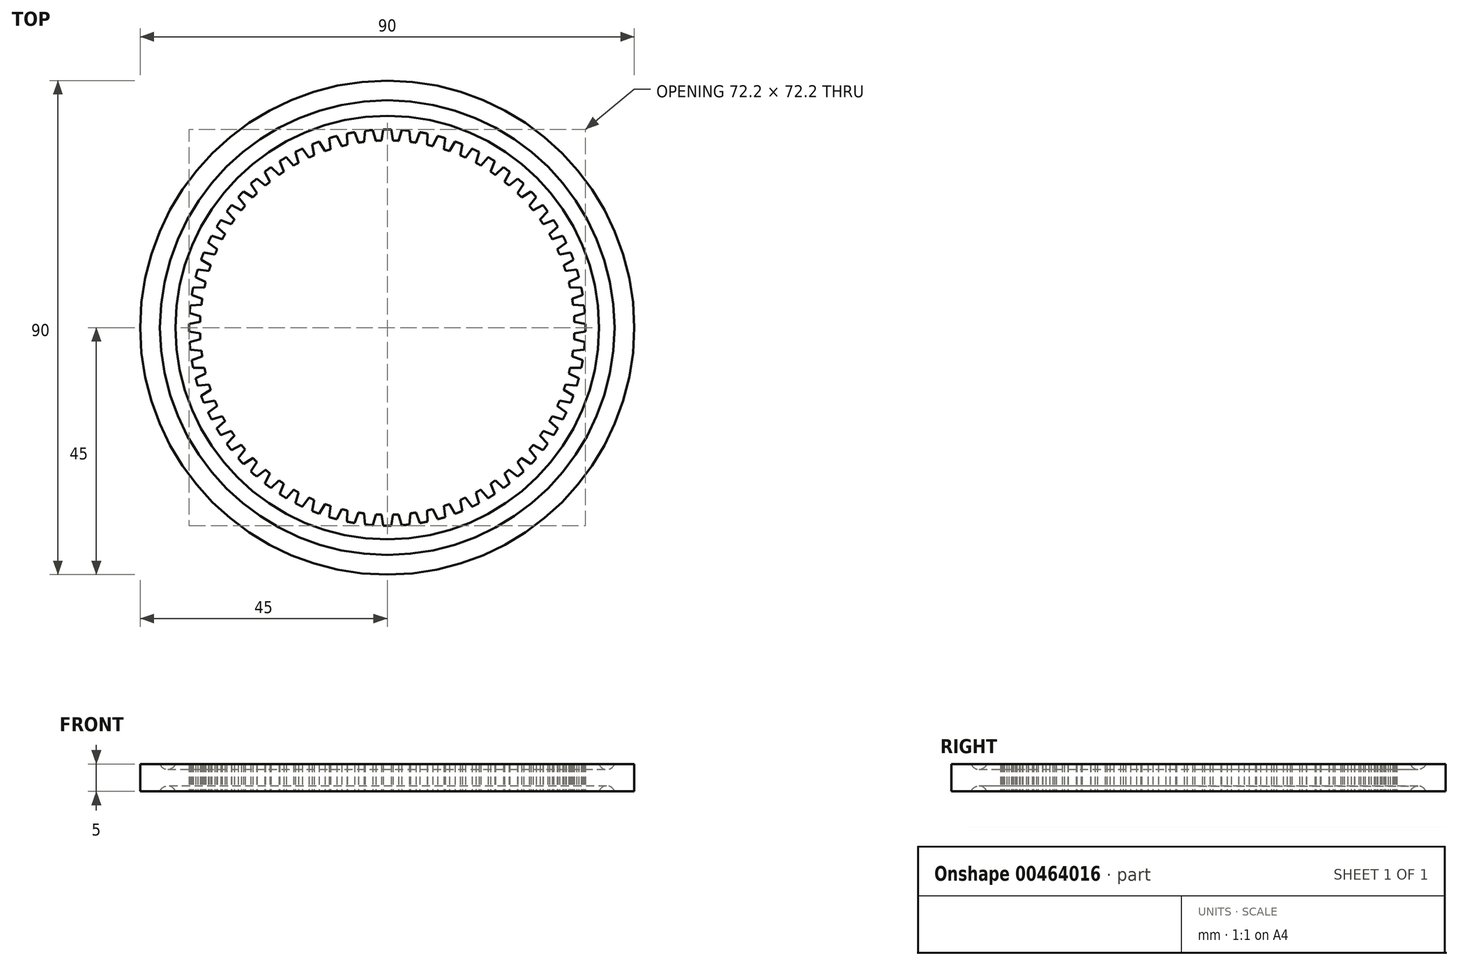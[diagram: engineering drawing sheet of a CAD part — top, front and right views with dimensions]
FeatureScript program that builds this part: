
annotation { "Feature Type Name" : "Feature", "Feature Type Description" : "" }
export const myFeature = defineFeature(function(context is Context, id is Id, definition is map)
    precondition{}
    {
        {
            var Q0;
            Q0=qCreatedBy(makeId("Top.planeOp"),FACE);
            var sketch = newSketch(context, id + "F0", { "sketchPlane" : qUnion([Q0])});
            skCircle(sketch, "E0", {"center": v(0, 0) * mm, "radius": 34.74 * mm, "construction": true});
            skCircle(sketch, "E1", {"center": v(0, 0) * mm, "radius": 45 * mm});
            skLineSegment(sketch, "E2", {"start": v(-0.94, 0) * mm, "end": v(-0.94, 34.7) * mm, "construction": true});
            skLineSegment(sketch, "E3", {"start": v(0.94, 0) * mm, "end": v(0.94, 34.7) * mm, "construction": true});
            skLineSegment(sketch, "E4", {"start": v(0, 0) * mm, "end": v(0, 34.8) * mm, "construction": true});
            skPoint(sketch, "E5", {"position": v(0.94, 34.73) * mm});
            skPoint(sketch, "E6", {"position": v(-0.94, 34.73) * mm});
            skLineSegment(sketch, "E7", {"start": v(0.94, 34.73) * mm, "end": v(1.06, 34.08) * mm});
            skLineSegment(sketch, "E8", {"start": v(0.94, 34.73) * mm, "end": v(0.7, 36.1) * mm});
            skLineSegment(sketch, "E9.MirrorCS", {"start": v(-0.94, 34.73) * mm, "end": v(-1.06, 34.08) * mm});
            skLineSegment(sketch, "E10.MirrorCS", {"start": v(-0.94, 34.73) * mm, "end": v(-0.7, 36.1) * mm});
            skLineSegment(sketch, "E11.1.0", {"start": v(-4.14, 34.5) * mm, "end": v(-4.2, 33.84) * mm});
            skLineSegment(sketch, "E11.1.1", {"start": v(-4.14, 34.5) * mm, "end": v(-4.03, 35.87) * mm});
            skLineSegment(sketch, "E11.1.2", {"start": v(-2.27, 34.67) * mm, "end": v(-2.63, 36) * mm});
            skLineSegment(sketch, "E11.1.3", {"start": v(-2.27, 34.67) * mm, "end": v(-2.1, 34.04) * mm});
            skLineSegment(sketch, "E11.2.0", {"start": v(-7.3, 33.96) * mm, "end": v(-7.3, 33.3) * mm});
            skLineSegment(sketch, "E11.2.1", {"start": v(-7.3, 33.96) * mm, "end": v(-7.32, 35.35) * mm});
            skLineSegment(sketch, "E11.2.2", {"start": v(-5.45, 34.3) * mm, "end": v(-5.94, 35.6) * mm});
            skLineSegment(sketch, "E11.2.3", {"start": v(-5.45, 34.3) * mm, "end": v(-5.22, 33.7) * mm});
            skLineSegment(sketch, "E11.3.0", {"start": v(-10.41, 33.14) * mm, "end": v(-10.34, 32.5) * mm});
            skLineSegment(sketch, "E11.3.1", {"start": v(-10.41, 33.14) * mm, "end": v(-10.55, 34.52) * mm});
            skLineSegment(sketch, "E11.3.2", {"start": v(-8.6, 33.66) * mm, "end": v(-9.2, 34.9) * mm});
            skLineSegment(sketch, "E11.3.3", {"start": v(-8.6, 33.66) * mm, "end": v(-8.31, 33.07) * mm});
            skLineSegment(sketch, "E11.4.0", {"start": v(-13.42, 32.04) * mm, "end": v(-13.3, 31.4) * mm});
            skLineSegment(sketch, "E11.4.1", {"start": v(-13.42, 32.04) * mm, "end": v(-13.7, 33.4) * mm});
            skLineSegment(sketch, "E11.4.2", {"start": v(-11.67, 32.72) * mm, "end": v(-12.38, 33.9) * mm});
            skLineSegment(sketch, "E11.4.3", {"start": v(-11.67, 32.72) * mm, "end": v(-11.33, 32.16) * mm});
            skLineSegment(sketch, "E11.5.0", {"start": v(-16.32, 30.67) * mm, "end": v(-16.14, 30.04) * mm});
            skLineSegment(sketch, "E11.5.1", {"start": v(-16.32, 30.67) * mm, "end": v(-16.72, 32) * mm});
            skLineSegment(sketch, "E11.5.2", {"start": v(-14.64, 31.5) * mm, "end": v(-15.46, 32.62) * mm});
            skLineSegment(sketch, "E11.5.3", {"start": v(-14.64, 31.5) * mm, "end": v(-14.25, 30.98) * mm});
            skLineSegment(sketch, "E11.6.0", {"start": v(-19.08, 29.03) * mm, "end": v(-18.84, 28.42) * mm});
            skLineSegment(sketch, "E11.6.1", {"start": v(-19.08, 29.03) * mm, "end": v(-19.6, 30.32) * mm});
            skLineSegment(sketch, "E11.6.2", {"start": v(-17.48, 30.02) * mm, "end": v(-18.4, 31.06) * mm});
            skLineSegment(sketch, "E11.6.3", {"start": v(-17.48, 30.02) * mm, "end": v(-17.04, 29.53) * mm});
            skLineSegment(sketch, "E11.7.0", {"start": v(-21.68, 27.15) * mm, "end": v(-21.38, 26.56) * mm});
            skLineSegment(sketch, "E11.7.1", {"start": v(-21.68, 27.15) * mm, "end": v(-22.31, 28.38) * mm});
            skLineSegment(sketch, "E11.7.2", {"start": v(-20.18, 28.28) * mm, "end": v(-21.2, 29.23) * mm});
            skLineSegment(sketch, "E11.7.3", {"start": v(-20.18, 28.28) * mm, "end": v(-19.7, 27.84) * mm});
            skLineSegment(sketch, "E11.8.0", {"start": v(-24.1, 25.03) * mm, "end": v(-23.74, 24.48) * mm});
            skLineSegment(sketch, "E11.8.1", {"start": v(-24.1, 25.03) * mm, "end": v(-24.83, 26.2) * mm});
            skLineSegment(sketch, "E11.8.2", {"start": v(-22.7, 26.3) * mm, "end": v(-23.8, 27.15) * mm});
            skLineSegment(sketch, "E11.8.3", {"start": v(-22.7, 26.3) * mm, "end": v(-22.18, 25.9) * mm});
            skLineSegment(sketch, "E11.9.0", {"start": v(-26.3, 22.7) * mm, "end": v(-25.9, 22.18) * mm});
            skLineSegment(sketch, "E11.9.1", {"start": v(-26.3, 22.7) * mm, "end": v(-27.15, 23.8) * mm});
            skLineSegment(sketch, "E11.9.2", {"start": v(-25.03, 24.1) * mm, "end": v(-26.2, 24.83) * mm});
            skLineSegment(sketch, "E11.9.3", {"start": v(-25.03, 24.1) * mm, "end": v(-24.48, 23.74) * mm});
            skLineSegment(sketch, "E11.10.0", {"start": v(-28.28, 20.18) * mm, "end": v(-27.84, 19.7) * mm});
            skLineSegment(sketch, "E11.10.1", {"start": v(-28.28, 20.18) * mm, "end": v(-29.23, 21.2) * mm});
            skLineSegment(sketch, "E11.10.2", {"start": v(-27.15, 21.68) * mm, "end": v(-28.38, 22.31) * mm});
            skLineSegment(sketch, "E11.10.3", {"start": v(-27.15, 21.68) * mm, "end": v(-26.56, 21.38) * mm});
            skLineSegment(sketch, "E11.11.0", {"start": v(-30.02, 17.48) * mm, "end": v(-29.53, 17.04) * mm});
            skLineSegment(sketch, "E11.11.1", {"start": v(-30.02, 17.48) * mm, "end": v(-31.06, 18.4) * mm});
            skLineSegment(sketch, "E11.11.2", {"start": v(-29.03, 19.08) * mm, "end": v(-30.32, 19.6) * mm});
            skLineSegment(sketch, "E11.11.3", {"start": v(-29.03, 19.08) * mm, "end": v(-28.42, 18.84) * mm});
            skLineSegment(sketch, "E11.12.0", {"start": v(-31.5, 14.64) * mm, "end": v(-30.98, 14.25) * mm});
            skLineSegment(sketch, "E11.12.1", {"start": v(-31.5, 14.64) * mm, "end": v(-32.62, 15.46) * mm});
            skLineSegment(sketch, "E11.12.2", {"start": v(-30.67, 16.32) * mm, "end": v(-32, 16.72) * mm});
            skLineSegment(sketch, "E11.12.3", {"start": v(-30.67, 16.32) * mm, "end": v(-30.04, 16.14) * mm});
            skLineSegment(sketch, "E11.13.0", {"start": v(-32.72, 11.67) * mm, "end": v(-32.16, 11.33) * mm});
            skLineSegment(sketch, "E11.13.1", {"start": v(-32.72, 11.67) * mm, "end": v(-33.9, 12.38) * mm});
            skLineSegment(sketch, "E11.13.2", {"start": v(-32.04, 13.42) * mm, "end": v(-33.4, 13.7) * mm});
            skLineSegment(sketch, "E11.13.3", {"start": v(-32.04, 13.42) * mm, "end": v(-31.4, 13.3) * mm});
            skLineSegment(sketch, "E11.14.0", {"start": v(-33.66, 8.6) * mm, "end": v(-33.07, 8.31) * mm});
            skLineSegment(sketch, "E11.14.1", {"start": v(-33.66, 8.6) * mm, "end": v(-34.9, 9.2) * mm});
            skLineSegment(sketch, "E11.14.2", {"start": v(-33.14, 10.41) * mm, "end": v(-34.52, 10.55) * mm});
            skLineSegment(sketch, "E11.14.3", {"start": v(-33.14, 10.41) * mm, "end": v(-32.5, 10.34) * mm});
            skLineSegment(sketch, "E11.15.0", {"start": v(-34.3, 5.45) * mm, "end": v(-33.7, 5.22) * mm});
            skLineSegment(sketch, "E11.15.1", {"start": v(-34.3, 5.45) * mm, "end": v(-35.6, 5.94) * mm});
            skLineSegment(sketch, "E11.15.2", {"start": v(-33.96, 7.3) * mm, "end": v(-35.35, 7.32) * mm});
            skLineSegment(sketch, "E11.15.3", {"start": v(-33.96, 7.3) * mm, "end": v(-33.3, 7.3) * mm});
            skLineSegment(sketch, "E11.16.0", {"start": v(-34.67, 2.27) * mm, "end": v(-34.04, 2.1) * mm});
            skLineSegment(sketch, "E11.16.1", {"start": v(-34.67, 2.27) * mm, "end": v(-36, 2.63) * mm});
            skLineSegment(sketch, "E11.16.2", {"start": v(-34.5, 4.14) * mm, "end": v(-35.87, 4.03) * mm});
            skLineSegment(sketch, "E11.16.3", {"start": v(-34.5, 4.14) * mm, "end": v(-33.84, 4.2) * mm});
            skLineSegment(sketch, "E11.17.0", {"start": v(-34.73, -0.94) * mm, "end": v(-34.08, -1.06) * mm});
            skLineSegment(sketch, "E11.17.1", {"start": v(-34.73, -0.94) * mm, "end": v(-36.1, -0.7) * mm});
            skLineSegment(sketch, "E11.17.2", {"start": v(-34.73, 0.94) * mm, "end": v(-36.1, 0.7) * mm});
            skLineSegment(sketch, "E11.17.3", {"start": v(-34.73, 0.94) * mm, "end": v(-34.08, 1.06) * mm});
            skLineSegment(sketch, "E11.18.0", {"start": v(-34.5, -4.14) * mm, "end": v(-33.84, -4.2) * mm});
            skLineSegment(sketch, "E11.18.1", {"start": v(-34.5, -4.14) * mm, "end": v(-35.87, -4.03) * mm});
            skLineSegment(sketch, "E11.18.2", {"start": v(-34.67, -2.27) * mm, "end": v(-36, -2.63) * mm});
            skLineSegment(sketch, "E11.18.3", {"start": v(-34.67, -2.27) * mm, "end": v(-34.04, -2.1) * mm});
            skLineSegment(sketch, "E11.19.0", {"start": v(-33.96, -7.3) * mm, "end": v(-33.3, -7.3) * mm});
            skLineSegment(sketch, "E11.19.1", {"start": v(-33.96, -7.3) * mm, "end": v(-35.35, -7.32) * mm});
            skLineSegment(sketch, "E11.19.2", {"start": v(-34.3, -5.45) * mm, "end": v(-35.6, -5.94) * mm});
            skLineSegment(sketch, "E11.19.3", {"start": v(-34.3, -5.45) * mm, "end": v(-33.7, -5.22) * mm});
            skLineSegment(sketch, "E11.20.0", {"start": v(-33.14, -10.41) * mm, "end": v(-32.5, -10.34) * mm});
            skLineSegment(sketch, "E11.20.1", {"start": v(-33.14, -10.41) * mm, "end": v(-34.52, -10.55) * mm});
            skLineSegment(sketch, "E11.20.2", {"start": v(-33.66, -8.6) * mm, "end": v(-34.9, -9.2) * mm});
            skLineSegment(sketch, "E11.20.3", {"start": v(-33.66, -8.6) * mm, "end": v(-33.07, -8.31) * mm});
            skLineSegment(sketch, "E11.21.0", {"start": v(-32.04, -13.42) * mm, "end": v(-31.4, -13.3) * mm});
            skLineSegment(sketch, "E11.21.1", {"start": v(-32.04, -13.42) * mm, "end": v(-33.4, -13.7) * mm});
            skLineSegment(sketch, "E11.21.2", {"start": v(-32.72, -11.67) * mm, "end": v(-33.9, -12.38) * mm});
            skLineSegment(sketch, "E11.21.3", {"start": v(-32.72, -11.67) * mm, "end": v(-32.16, -11.33) * mm});
            skLineSegment(sketch, "E11.22.0", {"start": v(-30.67, -16.32) * mm, "end": v(-30.04, -16.14) * mm});
            skLineSegment(sketch, "E11.22.1", {"start": v(-30.67, -16.32) * mm, "end": v(-32, -16.72) * mm});
            skLineSegment(sketch, "E11.22.2", {"start": v(-31.5, -14.64) * mm, "end": v(-32.62, -15.46) * mm});
            skLineSegment(sketch, "E11.22.3", {"start": v(-31.5, -14.64) * mm, "end": v(-30.98, -14.25) * mm});
            skLineSegment(sketch, "E11.23.0", {"start": v(-29.03, -19.08) * mm, "end": v(-28.42, -18.84) * mm});
            skLineSegment(sketch, "E11.23.1", {"start": v(-29.03, -19.08) * mm, "end": v(-30.32, -19.6) * mm});
            skLineSegment(sketch, "E11.23.2", {"start": v(-30.02, -17.48) * mm, "end": v(-31.06, -18.4) * mm});
            skLineSegment(sketch, "E11.23.3", {"start": v(-30.02, -17.48) * mm, "end": v(-29.53, -17.04) * mm});
            skLineSegment(sketch, "E11.24.0", {"start": v(-27.15, -21.68) * mm, "end": v(-26.56, -21.38) * mm});
            skLineSegment(sketch, "E11.24.1", {"start": v(-27.15, -21.68) * mm, "end": v(-28.38, -22.31) * mm});
            skLineSegment(sketch, "E11.24.2", {"start": v(-28.28, -20.18) * mm, "end": v(-29.23, -21.2) * mm});
            skLineSegment(sketch, "E11.24.3", {"start": v(-28.28, -20.18) * mm, "end": v(-27.84, -19.7) * mm});
            skLineSegment(sketch, "E11.25.0", {"start": v(-25.03, -24.1) * mm, "end": v(-24.48, -23.74) * mm});
            skLineSegment(sketch, "E11.25.1", {"start": v(-25.03, -24.1) * mm, "end": v(-26.2, -24.83) * mm});
            skLineSegment(sketch, "E11.25.2", {"start": v(-26.3, -22.7) * mm, "end": v(-27.15, -23.8) * mm});
            skLineSegment(sketch, "E11.25.3", {"start": v(-26.3, -22.7) * mm, "end": v(-25.9, -22.18) * mm});
            skLineSegment(sketch, "E11.26.0", {"start": v(-22.7, -26.3) * mm, "end": v(-22.18, -25.9) * mm});
            skLineSegment(sketch, "E11.26.1", {"start": v(-22.7, -26.3) * mm, "end": v(-23.8, -27.15) * mm});
            skLineSegment(sketch, "E11.26.2", {"start": v(-24.1, -25.03) * mm, "end": v(-24.83, -26.2) * mm});
            skLineSegment(sketch, "E11.26.3", {"start": v(-24.1, -25.03) * mm, "end": v(-23.74, -24.48) * mm});
            skLineSegment(sketch, "E11.27.0", {"start": v(-20.18, -28.28) * mm, "end": v(-19.7, -27.84) * mm});
            skLineSegment(sketch, "E11.27.1", {"start": v(-20.18, -28.28) * mm, "end": v(-21.2, -29.23) * mm});
            skLineSegment(sketch, "E11.27.2", {"start": v(-21.68, -27.15) * mm, "end": v(-22.31, -28.38) * mm});
            skLineSegment(sketch, "E11.27.3", {"start": v(-21.68, -27.15) * mm, "end": v(-21.38, -26.56) * mm});
            skLineSegment(sketch, "E11.28.0", {"start": v(-17.48, -30.02) * mm, "end": v(-17.04, -29.53) * mm});
            skLineSegment(sketch, "E11.28.1", {"start": v(-17.48, -30.02) * mm, "end": v(-18.4, -31.06) * mm});
            skLineSegment(sketch, "E11.28.2", {"start": v(-19.08, -29.03) * mm, "end": v(-19.6, -30.32) * mm});
            skLineSegment(sketch, "E11.28.3", {"start": v(-19.08, -29.03) * mm, "end": v(-18.84, -28.42) * mm});
            skLineSegment(sketch, "E11.29.0", {"start": v(-14.64, -31.5) * mm, "end": v(-14.25, -30.98) * mm});
            skLineSegment(sketch, "E11.29.1", {"start": v(-14.64, -31.5) * mm, "end": v(-15.46, -32.62) * mm});
            skLineSegment(sketch, "E11.29.2", {"start": v(-16.32, -30.67) * mm, "end": v(-16.72, -32) * mm});
            skLineSegment(sketch, "E11.29.3", {"start": v(-16.32, -30.67) * mm, "end": v(-16.14, -30.04) * mm});
            skLineSegment(sketch, "E11.30.0", {"start": v(-11.67, -32.72) * mm, "end": v(-11.33, -32.16) * mm});
            skLineSegment(sketch, "E11.30.1", {"start": v(-11.67, -32.72) * mm, "end": v(-12.38, -33.9) * mm});
            skLineSegment(sketch, "E11.30.2", {"start": v(-13.42, -32.04) * mm, "end": v(-13.7, -33.4) * mm});
            skLineSegment(sketch, "E11.30.3", {"start": v(-13.42, -32.04) * mm, "end": v(-13.3, -31.4) * mm});
            skLineSegment(sketch, "E11.31.0", {"start": v(-8.6, -33.66) * mm, "end": v(-8.31, -33.07) * mm});
            skLineSegment(sketch, "E11.31.1", {"start": v(-8.6, -33.66) * mm, "end": v(-9.2, -34.9) * mm});
            skLineSegment(sketch, "E11.31.2", {"start": v(-10.41, -33.14) * mm, "end": v(-10.55, -34.52) * mm});
            skLineSegment(sketch, "E11.31.3", {"start": v(-10.41, -33.14) * mm, "end": v(-10.34, -32.5) * mm});
            skLineSegment(sketch, "E11.32.0", {"start": v(-5.45, -34.3) * mm, "end": v(-5.22, -33.7) * mm});
            skLineSegment(sketch, "E11.32.1", {"start": v(-5.45, -34.3) * mm, "end": v(-5.94, -35.6) * mm});
            skLineSegment(sketch, "E11.32.2", {"start": v(-7.3, -33.96) * mm, "end": v(-7.32, -35.35) * mm});
            skLineSegment(sketch, "E11.32.3", {"start": v(-7.3, -33.96) * mm, "end": v(-7.3, -33.3) * mm});
            skLineSegment(sketch, "E11.33.0", {"start": v(-2.27, -34.67) * mm, "end": v(-2.1, -34.04) * mm});
            skLineSegment(sketch, "E11.33.1", {"start": v(-2.27, -34.67) * mm, "end": v(-2.63, -36) * mm});
            skLineSegment(sketch, "E11.33.2", {"start": v(-4.14, -34.5) * mm, "end": v(-4.03, -35.87) * mm});
            skLineSegment(sketch, "E11.33.3", {"start": v(-4.14, -34.5) * mm, "end": v(-4.2, -33.84) * mm});
            skLineSegment(sketch, "E11.34.0", {"start": v(0.94, -34.73) * mm, "end": v(1.06, -34.08) * mm});
            skLineSegment(sketch, "E11.34.1", {"start": v(0.94, -34.73) * mm, "end": v(0.7, -36.1) * mm});
            skLineSegment(sketch, "E11.34.2", {"start": v(-0.94, -34.73) * mm, "end": v(-0.7, -36.1) * mm});
            skLineSegment(sketch, "E11.34.3", {"start": v(-0.94, -34.73) * mm, "end": v(-1.06, -34.08) * mm});
            skLineSegment(sketch, "E11.35.0", {"start": v(4.14, -34.5) * mm, "end": v(4.2, -33.84) * mm});
            skLineSegment(sketch, "E11.35.1", {"start": v(4.14, -34.5) * mm, "end": v(4.03, -35.87) * mm});
            skLineSegment(sketch, "E11.35.2", {"start": v(2.27, -34.67) * mm, "end": v(2.63, -36) * mm});
            skLineSegment(sketch, "E11.35.3", {"start": v(2.27, -34.67) * mm, "end": v(2.1, -34.04) * mm});
            skLineSegment(sketch, "E11.36.0", {"start": v(7.3, -33.96) * mm, "end": v(7.3, -33.3) * mm});
            skLineSegment(sketch, "E11.36.1", {"start": v(7.3, -33.96) * mm, "end": v(7.32, -35.35) * mm});
            skLineSegment(sketch, "E11.36.2", {"start": v(5.45, -34.3) * mm, "end": v(5.94, -35.6) * mm});
            skLineSegment(sketch, "E11.36.3", {"start": v(5.45, -34.3) * mm, "end": v(5.22, -33.7) * mm});
            skLineSegment(sketch, "E11.37.0", {"start": v(10.41, -33.14) * mm, "end": v(10.34, -32.5) * mm});
            skLineSegment(sketch, "E11.37.1", {"start": v(10.41, -33.14) * mm, "end": v(10.55, -34.52) * mm});
            skLineSegment(sketch, "E11.37.2", {"start": v(8.6, -33.66) * mm, "end": v(9.2, -34.9) * mm});
            skLineSegment(sketch, "E11.37.3", {"start": v(8.6, -33.66) * mm, "end": v(8.31, -33.07) * mm});
            skLineSegment(sketch, "E11.38.0", {"start": v(13.42, -32.04) * mm, "end": v(13.3, -31.4) * mm});
            skLineSegment(sketch, "E11.38.1", {"start": v(13.42, -32.04) * mm, "end": v(13.7, -33.4) * mm});
            skLineSegment(sketch, "E11.38.2", {"start": v(11.67, -32.72) * mm, "end": v(12.38, -33.9) * mm});
            skLineSegment(sketch, "E11.38.3", {"start": v(11.67, -32.72) * mm, "end": v(11.33, -32.16) * mm});
            skLineSegment(sketch, "E11.39.0", {"start": v(16.32, -30.67) * mm, "end": v(16.14, -30.04) * mm});
            skLineSegment(sketch, "E11.39.1", {"start": v(16.32, -30.67) * mm, "end": v(16.72, -32) * mm});
            skLineSegment(sketch, "E11.39.2", {"start": v(14.64, -31.5) * mm, "end": v(15.46, -32.62) * mm});
            skLineSegment(sketch, "E11.39.3", {"start": v(14.64, -31.5) * mm, "end": v(14.25, -30.98) * mm});
            skLineSegment(sketch, "E11.40.0", {"start": v(19.08, -29.03) * mm, "end": v(18.84, -28.42) * mm});
            skLineSegment(sketch, "E11.40.1", {"start": v(19.08, -29.03) * mm, "end": v(19.6, -30.32) * mm});
            skLineSegment(sketch, "E11.40.2", {"start": v(17.48, -30.02) * mm, "end": v(18.4, -31.06) * mm});
            skLineSegment(sketch, "E11.40.3", {"start": v(17.48, -30.02) * mm, "end": v(17.04, -29.53) * mm});
            skLineSegment(sketch, "E11.41.0", {"start": v(21.68, -27.15) * mm, "end": v(21.38, -26.56) * mm});
            skLineSegment(sketch, "E11.41.1", {"start": v(21.68, -27.15) * mm, "end": v(22.31, -28.38) * mm});
            skLineSegment(sketch, "E11.41.2", {"start": v(20.18, -28.28) * mm, "end": v(21.2, -29.23) * mm});
            skLineSegment(sketch, "E11.41.3", {"start": v(20.18, -28.28) * mm, "end": v(19.7, -27.84) * mm});
            skLineSegment(sketch, "E11.42.0", {"start": v(24.1, -25.03) * mm, "end": v(23.74, -24.48) * mm});
            skLineSegment(sketch, "E11.42.1", {"start": v(24.1, -25.03) * mm, "end": v(24.83, -26.2) * mm});
            skLineSegment(sketch, "E11.42.2", {"start": v(22.7, -26.3) * mm, "end": v(23.8, -27.15) * mm});
            skLineSegment(sketch, "E11.42.3", {"start": v(22.7, -26.3) * mm, "end": v(22.18, -25.9) * mm});
            skLineSegment(sketch, "E11.43.0", {"start": v(26.3, -22.7) * mm, "end": v(25.9, -22.18) * mm});
            skLineSegment(sketch, "E11.43.1", {"start": v(26.3, -22.7) * mm, "end": v(27.15, -23.8) * mm});
            skLineSegment(sketch, "E11.43.2", {"start": v(25.03, -24.1) * mm, "end": v(26.2, -24.83) * mm});
            skLineSegment(sketch, "E11.43.3", {"start": v(25.03, -24.1) * mm, "end": v(24.48, -23.74) * mm});
            skLineSegment(sketch, "E11.44.0", {"start": v(28.28, -20.18) * mm, "end": v(27.84, -19.7) * mm});
            skLineSegment(sketch, "E11.44.1", {"start": v(28.28, -20.18) * mm, "end": v(29.23, -21.2) * mm});
            skLineSegment(sketch, "E11.44.2", {"start": v(27.15, -21.68) * mm, "end": v(28.38, -22.31) * mm});
            skLineSegment(sketch, "E11.44.3", {"start": v(27.15, -21.68) * mm, "end": v(26.56, -21.38) * mm});
            skLineSegment(sketch, "E11.45.0", {"start": v(30.02, -17.48) * mm, "end": v(29.53, -17.04) * mm});
            skLineSegment(sketch, "E11.45.1", {"start": v(30.02, -17.48) * mm, "end": v(31.06, -18.4) * mm});
            skLineSegment(sketch, "E11.45.2", {"start": v(29.03, -19.08) * mm, "end": v(30.32, -19.6) * mm});
            skLineSegment(sketch, "E11.45.3", {"start": v(29.03, -19.08) * mm, "end": v(28.42, -18.84) * mm});
            skLineSegment(sketch, "E11.46.0", {"start": v(31.5, -14.64) * mm, "end": v(30.98, -14.25) * mm});
            skLineSegment(sketch, "E11.46.1", {"start": v(31.5, -14.64) * mm, "end": v(32.62, -15.46) * mm});
            skLineSegment(sketch, "E11.46.2", {"start": v(30.67, -16.32) * mm, "end": v(32, -16.72) * mm});
            skLineSegment(sketch, "E11.46.3", {"start": v(30.67, -16.32) * mm, "end": v(30.04, -16.14) * mm});
            skLineSegment(sketch, "E11.47.0", {"start": v(32.72, -11.67) * mm, "end": v(32.16, -11.33) * mm});
            skLineSegment(sketch, "E11.47.1", {"start": v(32.72, -11.67) * mm, "end": v(33.9, -12.38) * mm});
            skLineSegment(sketch, "E11.47.2", {"start": v(32.04, -13.42) * mm, "end": v(33.4, -13.7) * mm});
            skLineSegment(sketch, "E11.47.3", {"start": v(32.04, -13.42) * mm, "end": v(31.4, -13.3) * mm});
            skLineSegment(sketch, "E11.48.0", {"start": v(33.66, -8.6) * mm, "end": v(33.07, -8.31) * mm});
            skLineSegment(sketch, "E11.48.1", {"start": v(33.66, -8.6) * mm, "end": v(34.9, -9.2) * mm});
            skLineSegment(sketch, "E11.48.2", {"start": v(33.14, -10.41) * mm, "end": v(34.52, -10.55) * mm});
            skLineSegment(sketch, "E11.48.3", {"start": v(33.14, -10.41) * mm, "end": v(32.5, -10.34) * mm});
            skLineSegment(sketch, "E11.49.0", {"start": v(34.3, -5.45) * mm, "end": v(33.7, -5.22) * mm});
            skLineSegment(sketch, "E11.49.1", {"start": v(34.3, -5.45) * mm, "end": v(35.6, -5.94) * mm});
            skLineSegment(sketch, "E11.49.2", {"start": v(33.96, -7.3) * mm, "end": v(35.35, -7.32) * mm});
            skLineSegment(sketch, "E11.49.3", {"start": v(33.96, -7.3) * mm, "end": v(33.3, -7.3) * mm});
            skLineSegment(sketch, "E11.50.0", {"start": v(34.67, -2.27) * mm, "end": v(34.04, -2.1) * mm});
            skLineSegment(sketch, "E11.50.1", {"start": v(34.67, -2.27) * mm, "end": v(36, -2.63) * mm});
            skLineSegment(sketch, "E11.50.2", {"start": v(34.5, -4.14) * mm, "end": v(35.87, -4.03) * mm});
            skLineSegment(sketch, "E11.50.3", {"start": v(34.5, -4.14) * mm, "end": v(33.84, -4.2) * mm});
            skLineSegment(sketch, "E11.51.0", {"start": v(34.73, 0.94) * mm, "end": v(34.08, 1.06) * mm});
            skLineSegment(sketch, "E11.51.1", {"start": v(34.73, 0.94) * mm, "end": v(36.1, 0.7) * mm});
            skLineSegment(sketch, "E11.51.2", {"start": v(34.73, -0.94) * mm, "end": v(36.1, -0.7) * mm});
            skLineSegment(sketch, "E11.51.3", {"start": v(34.73, -0.94) * mm, "end": v(34.08, -1.06) * mm});
            skLineSegment(sketch, "E11.52.0", {"start": v(34.5, 4.14) * mm, "end": v(33.84, 4.2) * mm});
            skLineSegment(sketch, "E11.52.1", {"start": v(34.5, 4.14) * mm, "end": v(35.87, 4.03) * mm});
            skLineSegment(sketch, "E11.52.2", {"start": v(34.67, 2.27) * mm, "end": v(36, 2.63) * mm});
            skLineSegment(sketch, "E11.52.3", {"start": v(34.67, 2.27) * mm, "end": v(34.04, 2.1) * mm});
            skLineSegment(sketch, "E11.53.0", {"start": v(33.96, 7.3) * mm, "end": v(33.3, 7.3) * mm});
            skLineSegment(sketch, "E11.53.1", {"start": v(33.96, 7.3) * mm, "end": v(35.35, 7.32) * mm});
            skLineSegment(sketch, "E11.53.2", {"start": v(34.3, 5.45) * mm, "end": v(35.6, 5.94) * mm});
            skLineSegment(sketch, "E11.53.3", {"start": v(34.3, 5.45) * mm, "end": v(33.7, 5.22) * mm});
            skLineSegment(sketch, "E11.54.0", {"start": v(33.14, 10.41) * mm, "end": v(32.5, 10.34) * mm});
            skLineSegment(sketch, "E11.54.1", {"start": v(33.14, 10.41) * mm, "end": v(34.52, 10.55) * mm});
            skLineSegment(sketch, "E11.54.2", {"start": v(33.66, 8.6) * mm, "end": v(34.9, 9.2) * mm});
            skLineSegment(sketch, "E11.54.3", {"start": v(33.66, 8.6) * mm, "end": v(33.07, 8.31) * mm});
            skLineSegment(sketch, "E11.55.0", {"start": v(32.04, 13.42) * mm, "end": v(31.4, 13.3) * mm});
            skLineSegment(sketch, "E11.55.1", {"start": v(32.04, 13.42) * mm, "end": v(33.4, 13.7) * mm});
            skLineSegment(sketch, "E11.55.2", {"start": v(32.72, 11.67) * mm, "end": v(33.9, 12.38) * mm});
            skLineSegment(sketch, "E11.55.3", {"start": v(32.72, 11.67) * mm, "end": v(32.16, 11.33) * mm});
            skLineSegment(sketch, "E11.56.0", {"start": v(30.67, 16.32) * mm, "end": v(30.04, 16.14) * mm});
            skLineSegment(sketch, "E11.56.1", {"start": v(30.67, 16.32) * mm, "end": v(32, 16.72) * mm});
            skLineSegment(sketch, "E11.56.2", {"start": v(31.5, 14.64) * mm, "end": v(32.62, 15.46) * mm});
            skLineSegment(sketch, "E11.56.3", {"start": v(31.5, 14.64) * mm, "end": v(30.98, 14.25) * mm});
            skLineSegment(sketch, "E11.57.0", {"start": v(29.03, 19.08) * mm, "end": v(28.42, 18.84) * mm});
            skLineSegment(sketch, "E11.57.1", {"start": v(29.03, 19.08) * mm, "end": v(30.32, 19.6) * mm});
            skLineSegment(sketch, "E11.57.2", {"start": v(30.02, 17.48) * mm, "end": v(31.06, 18.4) * mm});
            skLineSegment(sketch, "E11.57.3", {"start": v(30.02, 17.48) * mm, "end": v(29.53, 17.04) * mm});
            skLineSegment(sketch, "E11.58.0", {"start": v(27.15, 21.68) * mm, "end": v(26.56, 21.38) * mm});
            skLineSegment(sketch, "E11.58.1", {"start": v(27.15, 21.68) * mm, "end": v(28.38, 22.31) * mm});
            skLineSegment(sketch, "E11.58.2", {"start": v(28.28, 20.18) * mm, "end": v(29.23, 21.2) * mm});
            skLineSegment(sketch, "E11.58.3", {"start": v(28.28, 20.18) * mm, "end": v(27.84, 19.7) * mm});
            skLineSegment(sketch, "E11.59.0", {"start": v(25.03, 24.1) * mm, "end": v(24.48, 23.74) * mm});
            skLineSegment(sketch, "E11.59.1", {"start": v(25.03, 24.1) * mm, "end": v(26.2, 24.83) * mm});
            skLineSegment(sketch, "E11.59.2", {"start": v(26.3, 22.7) * mm, "end": v(27.15, 23.8) * mm});
            skLineSegment(sketch, "E11.59.3", {"start": v(26.3, 22.7) * mm, "end": v(25.9, 22.18) * mm});
            skLineSegment(sketch, "E11.60.0", {"start": v(22.7, 26.3) * mm, "end": v(22.18, 25.9) * mm});
            skLineSegment(sketch, "E11.60.1", {"start": v(22.7, 26.3) * mm, "end": v(23.8, 27.15) * mm});
            skLineSegment(sketch, "E11.60.2", {"start": v(24.1, 25.03) * mm, "end": v(24.83, 26.2) * mm});
            skLineSegment(sketch, "E11.60.3", {"start": v(24.1, 25.03) * mm, "end": v(23.74, 24.48) * mm});
            skLineSegment(sketch, "E11.61.0", {"start": v(20.18, 28.28) * mm, "end": v(19.7, 27.84) * mm});
            skLineSegment(sketch, "E11.61.1", {"start": v(20.18, 28.28) * mm, "end": v(21.2, 29.23) * mm});
            skLineSegment(sketch, "E11.61.2", {"start": v(21.68, 27.15) * mm, "end": v(22.31, 28.38) * mm});
            skLineSegment(sketch, "E11.61.3", {"start": v(21.68, 27.15) * mm, "end": v(21.38, 26.56) * mm});
            skLineSegment(sketch, "E11.62.0", {"start": v(17.48, 30.02) * mm, "end": v(17.04, 29.53) * mm});
            skLineSegment(sketch, "E11.62.1", {"start": v(17.48, 30.02) * mm, "end": v(18.4, 31.06) * mm});
            skLineSegment(sketch, "E11.62.2", {"start": v(19.08, 29.03) * mm, "end": v(19.6, 30.32) * mm});
            skLineSegment(sketch, "E11.62.3", {"start": v(19.08, 29.03) * mm, "end": v(18.84, 28.42) * mm});
            skLineSegment(sketch, "E11.63.0", {"start": v(14.64, 31.5) * mm, "end": v(14.25, 30.98) * mm});
            skLineSegment(sketch, "E11.63.1", {"start": v(14.64, 31.5) * mm, "end": v(15.46, 32.62) * mm});
            skLineSegment(sketch, "E11.63.2", {"start": v(16.32, 30.67) * mm, "end": v(16.72, 32) * mm});
            skLineSegment(sketch, "E11.63.3", {"start": v(16.32, 30.67) * mm, "end": v(16.14, 30.04) * mm});
            skLineSegment(sketch, "E11.64.0", {"start": v(11.67, 32.72) * mm, "end": v(11.33, 32.16) * mm});
            skLineSegment(sketch, "E11.64.1", {"start": v(11.67, 32.72) * mm, "end": v(12.38, 33.9) * mm});
            skLineSegment(sketch, "E11.64.2", {"start": v(13.42, 32.04) * mm, "end": v(13.7, 33.4) * mm});
            skLineSegment(sketch, "E11.64.3", {"start": v(13.42, 32.04) * mm, "end": v(13.3, 31.4) * mm});
            skLineSegment(sketch, "E11.65.0", {"start": v(8.6, 33.66) * mm, "end": v(8.31, 33.07) * mm});
            skLineSegment(sketch, "E11.65.1", {"start": v(8.6, 33.66) * mm, "end": v(9.2, 34.9) * mm});
            skLineSegment(sketch, "E11.65.2", {"start": v(10.41, 33.14) * mm, "end": v(10.55, 34.52) * mm});
            skLineSegment(sketch, "E11.65.3", {"start": v(10.41, 33.14) * mm, "end": v(10.34, 32.5) * mm});
            skLineSegment(sketch, "E11.66.0", {"start": v(5.45, 34.3) * mm, "end": v(5.22, 33.7) * mm});
            skLineSegment(sketch, "E11.66.1", {"start": v(5.45, 34.3) * mm, "end": v(5.94, 35.6) * mm});
            skLineSegment(sketch, "E11.66.2", {"start": v(7.3, 33.96) * mm, "end": v(7.32, 35.35) * mm});
            skLineSegment(sketch, "E11.66.3", {"start": v(7.3, 33.96) * mm, "end": v(7.3, 33.3) * mm});
            skLineSegment(sketch, "E11.67.0", {"start": v(2.27, 34.67) * mm, "end": v(2.1, 34.04) * mm});
            skLineSegment(sketch, "E11.67.1", {"start": v(2.27, 34.67) * mm, "end": v(2.63, 36) * mm});
            skLineSegment(sketch, "E11.67.2", {"start": v(4.14, 34.5) * mm, "end": v(4.03, 35.87) * mm});
            skLineSegment(sketch, "E11.67.3", {"start": v(4.14, 34.5) * mm, "end": v(4.2, 33.84) * mm});
            skArc(sketch, "E12", {"start": v(-0.7, 36.1) * mm, "mid": v(0, 36.1) * mm, "end": v(0.7, 36.1) * mm});
            skArc(sketch, "E13", {"start": v(1.06, 34.08) * mm, "mid": v(1.57, 34.06) * mm, "end": v(2.1, 34.04) * mm});
            skArc(sketch, "E14.1.0", {"start": v(-4.03, 35.87) * mm, "mid": v(-3.33, 35.95) * mm, "end": v(-2.63, 36) * mm});
            skArc(sketch, "E14.1.1", {"start": v(-2.1, 34.04) * mm, "mid": v(-1.57, 34.06) * mm, "end": v(-1.06, 34.08) * mm});
            skArc(sketch, "E14.2.0", {"start": v(-7.32, 35.35) * mm, "mid": v(-6.63, 35.49) * mm, "end": v(-5.94, 35.6) * mm});
            skArc(sketch, "E14.2.1", {"start": v(-5.22, 33.7) * mm, "mid": v(-4.71, 33.77) * mm, "end": v(-4.2, 33.84) * mm});
            skArc(sketch, "E14.3.0", {"start": v(-10.55, 34.52) * mm, "mid": v(-9.88, 34.72) * mm, "end": v(-9.2, 34.9) * mm});
            skArc(sketch, "E14.3.1", {"start": v(-8.31, 33.07) * mm, "mid": v(-7.8, 33.2) * mm, "end": v(-7.3, 33.3) * mm});
            skArc(sketch, "E14.4.0", {"start": v(-13.7, 33.4) * mm, "mid": v(-13.04, 33.66) * mm, "end": v(-12.38, 33.9) * mm});
            skArc(sketch, "E14.4.1", {"start": v(-11.33, 32.16) * mm, "mid": v(-10.84, 32.33) * mm, "end": v(-10.34, 32.5) * mm});
            skArc(sketch, "E14.5.0", {"start": v(-16.72, 32) * mm, "mid": v(-16.1, 32.32) * mm, "end": v(-15.46, 32.62) * mm});
            skArc(sketch, "E14.5.1", {"start": v(-14.25, 30.98) * mm, "mid": v(-13.77, 31.2) * mm, "end": v(-13.3, 31.4) * mm});
            skArc(sketch, "E14.6.0", {"start": v(-19.6, 30.32) * mm, "mid": v(-19, 30.7) * mm, "end": v(-18.4, 31.06) * mm});
            skArc(sketch, "E14.6.1", {"start": v(-17.04, 29.53) * mm, "mid": v(-16.6, 29.8) * mm, "end": v(-16.14, 30.04) * mm});
            skArc(sketch, "E14.7.0", {"start": v(-22.31, 28.38) * mm, "mid": v(-21.76, 28.8) * mm, "end": v(-21.2, 29.23) * mm});
            skArc(sketch, "E14.7.1", {"start": v(-19.7, 27.84) * mm, "mid": v(-19.27, 28.13) * mm, "end": v(-18.84, 28.42) * mm});
            skArc(sketch, "E14.8.0", {"start": v(-24.83, 26.2) * mm, "mid": v(-24.32, 26.68) * mm, "end": v(-23.8, 27.15) * mm});
            skArc(sketch, "E14.8.1", {"start": v(-22.18, 25.9) * mm, "mid": v(-21.78, 26.23) * mm, "end": v(-21.38, 26.56) * mm});
            skArc(sketch, "E14.9.0", {"start": v(-27.15, 23.8) * mm, "mid": v(-26.68, 24.32) * mm, "end": v(-26.2, 24.83) * mm});
            skArc(sketch, "E14.9.1", {"start": v(-24.48, 23.74) * mm, "mid": v(-24.11, 24.11) * mm, "end": v(-23.74, 24.48) * mm});
            skArc(sketch, "E14.10.0", {"start": v(-29.23, 21.2) * mm, "mid": v(-28.8, 21.76) * mm, "end": v(-28.38, 22.31) * mm});
            skArc(sketch, "E14.10.1", {"start": v(-26.56, 21.38) * mm, "mid": v(-26.23, 21.78) * mm, "end": v(-25.9, 22.18) * mm});
            skArc(sketch, "E14.11.0", {"start": v(-31.06, 18.4) * mm, "mid": v(-30.7, 19) * mm, "end": v(-30.32, 19.6) * mm});
            skArc(sketch, "E14.11.1", {"start": v(-28.42, 18.84) * mm, "mid": v(-28.13, 19.27) * mm, "end": v(-27.84, 19.7) * mm});
            skArc(sketch, "E14.12.0", {"start": v(-32.62, 15.46) * mm, "mid": v(-32.32, 16.1) * mm, "end": v(-32, 16.72) * mm});
            skArc(sketch, "E14.12.1", {"start": v(-30.04, 16.14) * mm, "mid": v(-29.8, 16.6) * mm, "end": v(-29.53, 17.04) * mm});
            skArc(sketch, "E14.13.0", {"start": v(-33.9, 12.38) * mm, "mid": v(-33.66, 13.04) * mm, "end": v(-33.4, 13.7) * mm});
            skArc(sketch, "E14.13.1", {"start": v(-31.4, 13.3) * mm, "mid": v(-31.2, 13.77) * mm, "end": v(-30.98, 14.25) * mm});
            skArc(sketch, "E14.14.0", {"start": v(-34.9, 9.2) * mm, "mid": v(-34.72, 9.88) * mm, "end": v(-34.52, 10.55) * mm});
            skArc(sketch, "E14.14.1", {"start": v(-32.5, 10.34) * mm, "mid": v(-32.33, 10.84) * mm, "end": v(-32.16, 11.33) * mm});
            skArc(sketch, "E14.15.0", {"start": v(-35.6, 5.94) * mm, "mid": v(-35.49, 6.63) * mm, "end": v(-35.35, 7.32) * mm});
            skArc(sketch, "E14.15.1", {"start": v(-33.3, 7.3) * mm, "mid": v(-33.2, 7.8) * mm, "end": v(-33.07, 8.31) * mm});
            skArc(sketch, "E14.16.0", {"start": v(-36, 2.63) * mm, "mid": v(-35.95, 3.33) * mm, "end": v(-35.87, 4.03) * mm});
            skArc(sketch, "E14.16.1", {"start": v(-33.84, 4.2) * mm, "mid": v(-33.77, 4.71) * mm, "end": v(-33.7, 5.22) * mm});
            skArc(sketch, "E14.17.0", {"start": v(-36.1, -0.7) * mm, "mid": v(-36.1, 0) * mm, "end": v(-36.1, 0.7) * mm});
            skArc(sketch, "E14.17.1", {"start": v(-34.08, 1.06) * mm, "mid": v(-34.06, 1.57) * mm, "end": v(-34.04, 2.1) * mm});
            skArc(sketch, "E14.18.0", {"start": v(-35.87, -4.03) * mm, "mid": v(-35.95, -3.33) * mm, "end": v(-36, -2.63) * mm});
            skArc(sketch, "E14.18.1", {"start": v(-34.04, -2.1) * mm, "mid": v(-34.06, -1.57) * mm, "end": v(-34.08, -1.06) * mm});
            skArc(sketch, "E14.19.0", {"start": v(-35.35, -7.32) * mm, "mid": v(-35.49, -6.63) * mm, "end": v(-35.6, -5.94) * mm});
            skArc(sketch, "E14.19.1", {"start": v(-33.7, -5.22) * mm, "mid": v(-33.77, -4.71) * mm, "end": v(-33.84, -4.2) * mm});
            skArc(sketch, "E14.20.0", {"start": v(-34.52, -10.55) * mm, "mid": v(-34.72, -9.88) * mm, "end": v(-34.9, -9.2) * mm});
            skArc(sketch, "E14.20.1", {"start": v(-33.07, -8.31) * mm, "mid": v(-33.2, -7.8) * mm, "end": v(-33.3, -7.3) * mm});
            skArc(sketch, "E14.21.0", {"start": v(-33.4, -13.7) * mm, "mid": v(-33.66, -13.04) * mm, "end": v(-33.9, -12.38) * mm});
            skArc(sketch, "E14.21.1", {"start": v(-32.16, -11.33) * mm, "mid": v(-32.33, -10.84) * mm, "end": v(-32.5, -10.34) * mm});
            skArc(sketch, "E14.22.0", {"start": v(-32, -16.72) * mm, "mid": v(-32.32, -16.1) * mm, "end": v(-32.62, -15.46) * mm});
            skArc(sketch, "E14.22.1", {"start": v(-30.98, -14.25) * mm, "mid": v(-31.2, -13.77) * mm, "end": v(-31.4, -13.3) * mm});
            skArc(sketch, "E14.23.0", {"start": v(-30.32, -19.6) * mm, "mid": v(-30.7, -19) * mm, "end": v(-31.06, -18.4) * mm});
            skArc(sketch, "E14.23.1", {"start": v(-29.53, -17.04) * mm, "mid": v(-29.8, -16.6) * mm, "end": v(-30.04, -16.14) * mm});
            skArc(sketch, "E14.24.0", {"start": v(-28.38, -22.31) * mm, "mid": v(-28.8, -21.76) * mm, "end": v(-29.23, -21.2) * mm});
            skArc(sketch, "E14.24.1", {"start": v(-27.84, -19.7) * mm, "mid": v(-28.13, -19.27) * mm, "end": v(-28.42, -18.84) * mm});
            skArc(sketch, "E14.25.0", {"start": v(-26.2, -24.83) * mm, "mid": v(-26.68, -24.32) * mm, "end": v(-27.15, -23.8) * mm});
            skArc(sketch, "E14.25.1", {"start": v(-25.9, -22.18) * mm, "mid": v(-26.23, -21.78) * mm, "end": v(-26.56, -21.38) * mm});
            skArc(sketch, "E14.26.0", {"start": v(-23.8, -27.15) * mm, "mid": v(-24.32, -26.68) * mm, "end": v(-24.83, -26.2) * mm});
            skArc(sketch, "E14.26.1", {"start": v(-23.74, -24.48) * mm, "mid": v(-24.11, -24.11) * mm, "end": v(-24.48, -23.74) * mm});
            skArc(sketch, "E14.27.0", {"start": v(-21.2, -29.23) * mm, "mid": v(-21.76, -28.8) * mm, "end": v(-22.31, -28.38) * mm});
            skArc(sketch, "E14.27.1", {"start": v(-21.38, -26.56) * mm, "mid": v(-21.78, -26.23) * mm, "end": v(-22.18, -25.9) * mm});
            skArc(sketch, "E14.28.0", {"start": v(-18.4, -31.06) * mm, "mid": v(-19, -30.7) * mm, "end": v(-19.6, -30.32) * mm});
            skArc(sketch, "E14.28.1", {"start": v(-18.84, -28.42) * mm, "mid": v(-19.27, -28.13) * mm, "end": v(-19.7, -27.84) * mm});
            skArc(sketch, "E14.29.0", {"start": v(-15.46, -32.62) * mm, "mid": v(-16.1, -32.32) * mm, "end": v(-16.72, -32) * mm});
            skArc(sketch, "E14.29.1", {"start": v(-16.14, -30.04) * mm, "mid": v(-16.6, -29.8) * mm, "end": v(-17.04, -29.53) * mm});
            skArc(sketch, "E14.30.0", {"start": v(-12.38, -33.9) * mm, "mid": v(-13.04, -33.66) * mm, "end": v(-13.7, -33.4) * mm});
            skArc(sketch, "E14.30.1", {"start": v(-13.3, -31.4) * mm, "mid": v(-13.77, -31.2) * mm, "end": v(-14.25, -30.98) * mm});
            skArc(sketch, "E14.31.0", {"start": v(-9.2, -34.9) * mm, "mid": v(-9.88, -34.72) * mm, "end": v(-10.55, -34.52) * mm});
            skArc(sketch, "E14.31.1", {"start": v(-10.34, -32.5) * mm, "mid": v(-10.84, -32.33) * mm, "end": v(-11.33, -32.16) * mm});
            skArc(sketch, "E14.32.0", {"start": v(-5.94, -35.6) * mm, "mid": v(-6.63, -35.49) * mm, "end": v(-7.32, -35.35) * mm});
            skArc(sketch, "E14.32.1", {"start": v(-7.3, -33.3) * mm, "mid": v(-7.8, -33.2) * mm, "end": v(-8.31, -33.07) * mm});
            skArc(sketch, "E14.33.0", {"start": v(-2.63, -36) * mm, "mid": v(-3.33, -35.95) * mm, "end": v(-4.03, -35.87) * mm});
            skArc(sketch, "E14.33.1", {"start": v(-4.2, -33.84) * mm, "mid": v(-4.71, -33.77) * mm, "end": v(-5.22, -33.7) * mm});
            skArc(sketch, "E14.34.0", {"start": v(0.7, -36.1) * mm, "mid": v(0, -36.1) * mm, "end": v(-0.7, -36.1) * mm});
            skArc(sketch, "E14.34.1", {"start": v(-1.06, -34.08) * mm, "mid": v(-1.57, -34.06) * mm, "end": v(-2.1, -34.04) * mm});
            skArc(sketch, "E14.35.0", {"start": v(4.03, -35.87) * mm, "mid": v(3.33, -35.95) * mm, "end": v(2.63, -36) * mm});
            skArc(sketch, "E14.35.1", {"start": v(2.1, -34.04) * mm, "mid": v(1.57, -34.06) * mm, "end": v(1.06, -34.08) * mm});
            skArc(sketch, "E14.36.0", {"start": v(7.32, -35.35) * mm, "mid": v(6.63, -35.49) * mm, "end": v(5.94, -35.6) * mm});
            skArc(sketch, "E14.36.1", {"start": v(5.22, -33.7) * mm, "mid": v(4.71, -33.77) * mm, "end": v(4.2, -33.84) * mm});
            skArc(sketch, "E14.37.0", {"start": v(10.55, -34.52) * mm, "mid": v(9.88, -34.72) * mm, "end": v(9.2, -34.9) * mm});
            skArc(sketch, "E14.37.1", {"start": v(8.31, -33.07) * mm, "mid": v(7.8, -33.2) * mm, "end": v(7.3, -33.3) * mm});
            skArc(sketch, "E14.38.0", {"start": v(13.7, -33.4) * mm, "mid": v(13.04, -33.66) * mm, "end": v(12.38, -33.9) * mm});
            skArc(sketch, "E14.38.1", {"start": v(11.33, -32.16) * mm, "mid": v(10.84, -32.33) * mm, "end": v(10.34, -32.5) * mm});
            skArc(sketch, "E14.39.0", {"start": v(16.72, -32) * mm, "mid": v(16.1, -32.32) * mm, "end": v(15.46, -32.62) * mm});
            skArc(sketch, "E14.39.1", {"start": v(14.25, -30.98) * mm, "mid": v(13.77, -31.2) * mm, "end": v(13.3, -31.4) * mm});
            skArc(sketch, "E14.40.0", {"start": v(19.6, -30.32) * mm, "mid": v(19, -30.7) * mm, "end": v(18.4, -31.06) * mm});
            skArc(sketch, "E14.40.1", {"start": v(17.04, -29.53) * mm, "mid": v(16.6, -29.8) * mm, "end": v(16.14, -30.04) * mm});
            skArc(sketch, "E14.41.0", {"start": v(22.31, -28.38) * mm, "mid": v(21.76, -28.8) * mm, "end": v(21.2, -29.23) * mm});
            skArc(sketch, "E14.41.1", {"start": v(19.7, -27.84) * mm, "mid": v(19.27, -28.13) * mm, "end": v(18.84, -28.42) * mm});
            skArc(sketch, "E14.42.0", {"start": v(24.83, -26.2) * mm, "mid": v(24.32, -26.68) * mm, "end": v(23.8, -27.15) * mm});
            skArc(sketch, "E14.42.1", {"start": v(22.18, -25.9) * mm, "mid": v(21.78, -26.23) * mm, "end": v(21.38, -26.56) * mm});
            skArc(sketch, "E14.43.0", {"start": v(27.15, -23.8) * mm, "mid": v(26.68, -24.32) * mm, "end": v(26.2, -24.83) * mm});
            skArc(sketch, "E14.43.1", {"start": v(24.48, -23.74) * mm, "mid": v(24.11, -24.11) * mm, "end": v(23.74, -24.48) * mm});
            skArc(sketch, "E14.44.0", {"start": v(29.23, -21.2) * mm, "mid": v(28.8, -21.76) * mm, "end": v(28.38, -22.31) * mm});
            skArc(sketch, "E14.44.1", {"start": v(26.56, -21.38) * mm, "mid": v(26.23, -21.78) * mm, "end": v(25.9, -22.18) * mm});
            skArc(sketch, "E14.45.0", {"start": v(31.06, -18.4) * mm, "mid": v(30.7, -19) * mm, "end": v(30.32, -19.6) * mm});
            skArc(sketch, "E14.45.1", {"start": v(28.42, -18.84) * mm, "mid": v(28.13, -19.27) * mm, "end": v(27.84, -19.7) * mm});
            skArc(sketch, "E14.46.0", {"start": v(32.62, -15.46) * mm, "mid": v(32.32, -16.1) * mm, "end": v(32, -16.72) * mm});
            skArc(sketch, "E14.46.1", {"start": v(30.04, -16.14) * mm, "mid": v(29.8, -16.6) * mm, "end": v(29.53, -17.04) * mm});
            skArc(sketch, "E14.47.0", {"start": v(33.9, -12.38) * mm, "mid": v(33.66, -13.04) * mm, "end": v(33.4, -13.7) * mm});
            skArc(sketch, "E14.47.1", {"start": v(31.4, -13.3) * mm, "mid": v(31.2, -13.77) * mm, "end": v(30.98, -14.25) * mm});
            skArc(sketch, "E14.48.0", {"start": v(34.9, -9.2) * mm, "mid": v(34.72, -9.88) * mm, "end": v(34.52, -10.55) * mm});
            skArc(sketch, "E14.48.1", {"start": v(32.5, -10.34) * mm, "mid": v(32.33, -10.84) * mm, "end": v(32.16, -11.33) * mm});
            skArc(sketch, "E14.49.0", {"start": v(35.6, -5.94) * mm, "mid": v(35.49, -6.63) * mm, "end": v(35.35, -7.32) * mm});
            skArc(sketch, "E14.49.1", {"start": v(33.3, -7.3) * mm, "mid": v(33.2, -7.8) * mm, "end": v(33.07, -8.31) * mm});
            skArc(sketch, "E14.50.0", {"start": v(36, -2.63) * mm, "mid": v(35.95, -3.33) * mm, "end": v(35.87, -4.03) * mm});
            skArc(sketch, "E14.50.1", {"start": v(33.84, -4.2) * mm, "mid": v(33.77, -4.71) * mm, "end": v(33.7, -5.22) * mm});
            skArc(sketch, "E14.51.0", {"start": v(36.1, 0.7) * mm, "mid": v(36.1, 0) * mm, "end": v(36.1, -0.7) * mm});
            skArc(sketch, "E14.51.1", {"start": v(34.08, -1.06) * mm, "mid": v(34.06, -1.57) * mm, "end": v(34.04, -2.1) * mm});
            skArc(sketch, "E14.52.0", {"start": v(35.87, 4.03) * mm, "mid": v(35.95, 3.33) * mm, "end": v(36, 2.63) * mm});
            skArc(sketch, "E14.52.1", {"start": v(34.04, 2.1) * mm, "mid": v(34.06, 1.57) * mm, "end": v(34.08, 1.06) * mm});
            skArc(sketch, "E14.53.0", {"start": v(35.35, 7.32) * mm, "mid": v(35.49, 6.63) * mm, "end": v(35.6, 5.94) * mm});
            skArc(sketch, "E14.53.1", {"start": v(33.7, 5.22) * mm, "mid": v(33.77, 4.71) * mm, "end": v(33.84, 4.2) * mm});
            skArc(sketch, "E14.54.0", {"start": v(34.52, 10.55) * mm, "mid": v(34.72, 9.88) * mm, "end": v(34.9, 9.2) * mm});
            skArc(sketch, "E14.54.1", {"start": v(33.07, 8.31) * mm, "mid": v(33.2, 7.8) * mm, "end": v(33.3, 7.3) * mm});
            skArc(sketch, "E14.55.0", {"start": v(33.4, 13.7) * mm, "mid": v(33.66, 13.04) * mm, "end": v(33.9, 12.38) * mm});
            skArc(sketch, "E14.55.1", {"start": v(32.16, 11.33) * mm, "mid": v(32.33, 10.84) * mm, "end": v(32.5, 10.34) * mm});
            skArc(sketch, "E14.56.0", {"start": v(32, 16.72) * mm, "mid": v(32.32, 16.1) * mm, "end": v(32.62, 15.46) * mm});
            skArc(sketch, "E14.56.1", {"start": v(30.98, 14.25) * mm, "mid": v(31.2, 13.77) * mm, "end": v(31.4, 13.3) * mm});
            skArc(sketch, "E14.57.0", {"start": v(30.32, 19.6) * mm, "mid": v(30.7, 19) * mm, "end": v(31.06, 18.4) * mm});
            skArc(sketch, "E14.57.1", {"start": v(29.53, 17.04) * mm, "mid": v(29.8, 16.6) * mm, "end": v(30.04, 16.14) * mm});
            skArc(sketch, "E14.58.0", {"start": v(28.38, 22.31) * mm, "mid": v(28.8, 21.76) * mm, "end": v(29.23, 21.2) * mm});
            skArc(sketch, "E14.58.1", {"start": v(27.84, 19.7) * mm, "mid": v(28.13, 19.27) * mm, "end": v(28.42, 18.84) * mm});
            skArc(sketch, "E14.59.0", {"start": v(26.2, 24.83) * mm, "mid": v(26.68, 24.32) * mm, "end": v(27.15, 23.8) * mm});
            skArc(sketch, "E14.59.1", {"start": v(25.9, 22.18) * mm, "mid": v(26.23, 21.78) * mm, "end": v(26.56, 21.38) * mm});
            skArc(sketch, "E14.60.0", {"start": v(23.8, 27.15) * mm, "mid": v(24.32, 26.68) * mm, "end": v(24.83, 26.2) * mm});
            skArc(sketch, "E14.60.1", {"start": v(23.74, 24.48) * mm, "mid": v(24.11, 24.11) * mm, "end": v(24.48, 23.74) * mm});
            skArc(sketch, "E14.61.0", {"start": v(21.2, 29.23) * mm, "mid": v(21.76, 28.8) * mm, "end": v(22.31, 28.38) * mm});
            skArc(sketch, "E14.61.1", {"start": v(21.38, 26.56) * mm, "mid": v(21.78, 26.23) * mm, "end": v(22.18, 25.9) * mm});
            skArc(sketch, "E14.62.0", {"start": v(18.4, 31.06) * mm, "mid": v(19, 30.7) * mm, "end": v(19.6, 30.32) * mm});
            skArc(sketch, "E14.62.1", {"start": v(18.84, 28.42) * mm, "mid": v(19.27, 28.13) * mm, "end": v(19.7, 27.84) * mm});
            skArc(sketch, "E14.63.0", {"start": v(15.46, 32.62) * mm, "mid": v(16.1, 32.32) * mm, "end": v(16.72, 32) * mm});
            skArc(sketch, "E14.63.1", {"start": v(16.14, 30.04) * mm, "mid": v(16.6, 29.8) * mm, "end": v(17.04, 29.53) * mm});
            skArc(sketch, "E14.64.0", {"start": v(12.38, 33.9) * mm, "mid": v(13.04, 33.66) * mm, "end": v(13.7, 33.4) * mm});
            skArc(sketch, "E14.64.1", {"start": v(13.3, 31.4) * mm, "mid": v(13.77, 31.2) * mm, "end": v(14.25, 30.98) * mm});
            skArc(sketch, "E14.65.0", {"start": v(9.2, 34.9) * mm, "mid": v(9.88, 34.72) * mm, "end": v(10.55, 34.52) * mm});
            skArc(sketch, "E14.65.1", {"start": v(10.34, 32.5) * mm, "mid": v(10.84, 32.33) * mm, "end": v(11.33, 32.16) * mm});
            skArc(sketch, "E14.66.0", {"start": v(5.94, 35.6) * mm, "mid": v(6.63, 35.49) * mm, "end": v(7.32, 35.35) * mm});
            skArc(sketch, "E14.66.1", {"start": v(7.3, 33.3) * mm, "mid": v(7.8, 33.2) * mm, "end": v(8.31, 33.07) * mm});
            skArc(sketch, "E14.67.0", {"start": v(2.63, 36) * mm, "mid": v(3.33, 35.95) * mm, "end": v(4.03, 35.87) * mm});
            skArc(sketch, "E14.67.1", {"start": v(4.2, 33.84) * mm, "mid": v(4.71, 33.77) * mm, "end": v(5.22, 33.7) * mm});
            skSolve(sketch);
        }
        {
            var Q0;
            Q0=makeQuery(id+"F0.imprint","IMPRINT",FACE,{"disambiguationData":[TD([[makeQuery(id+"F0.imprint","IMPRINT",EDGE,{"derivedFrom":sQuery(id+"F0.wireOp",EDGE,"E1")}),1.0]])]});
            extrude(context, id + "F1", {"entities" : qUnion([Q0]), "depth" : 5 * mm});
        }
        {
            var Q0;
            Q0=qCreatedBy(makeId("Front.planeOp"),FACE);
            var sketch = newSketch(context, id + "F2", { "sketchPlane" : qUnion([Q0])});
            skLineSegment(sketch, "E15", {"start": v(-45, 0) * mm, "end": v(-45, 5) * mm});
            skLineSegment(sketch, "E16", {"start": v(45, 5) * mm, "end": v(45, 0) * mm});
            skCircle(sketch, "E17", {"center": v(-40, 5.5) * mm, "radius": 1.5 * mm});
            skLineSegment(sketch, "E18", {"start": v(-45, 2.5) * mm, "end": v(-35.07, 2.5) * mm, "construction": true});
            skCircle(sketch, "E19.MirrorC", {"center": v(-40, -0.5) * mm, "radius": 1.5 * mm});
            skLineSegment(sketch, "E20.bottom", {"start": v(-45, 5) * mm, "end": v(-42, 5) * mm});
            skLineSegment(sketch, "E20.top", {"start": v(-45, 15) * mm, "end": v(-42, 15) * mm});
            skLineSegment(sketch, "E20.left", {"start": v(-45, 5) * mm, "end": v(-45, 15) * mm});
            skLineSegment(sketch, "E20.right", {"start": v(-42, 5) * mm, "end": v(-42, 15) * mm});
            skLineSegment(sketch, "E21.MirrorCS", {"start": v(-42, 0) * mm, "end": v(-42, -10) * mm});
            skLineSegment(sketch, "E22.MirrorCS", {"start": v(-45, 0) * mm, "end": v(-42, 0) * mm});
            skLineSegment(sketch, "E23.MirrorCS", {"start": v(-45, 0) * mm, "end": v(-45, -10) * mm});
            skLineSegment(sketch, "E24.MirrorCS", {"start": v(-45, -10) * mm, "end": v(-42, -10) * mm});
            skSolve(sketch);
        }
        {
            var Q0;
            Q0 = qSketchRegion(id + "F2", true);
            var Q1;
            Q1=makeQuery(id+"F1.opExtrude","CAP_EDGE",EDGE,{"disambiguationData":[OSD([sQuery(id+"F0.wireOp",EDGE,"E1")])],"isStart":false});
            revolve(context, id + "F3", {"operationType" : NewBodyOperationType.REMOVE, "entities" : qUnion([Q0]), "axis" : qUnion([Q1]), "revolveType" : RevolveType.FULL, "oppositeDirection" : true});
        }
    });
